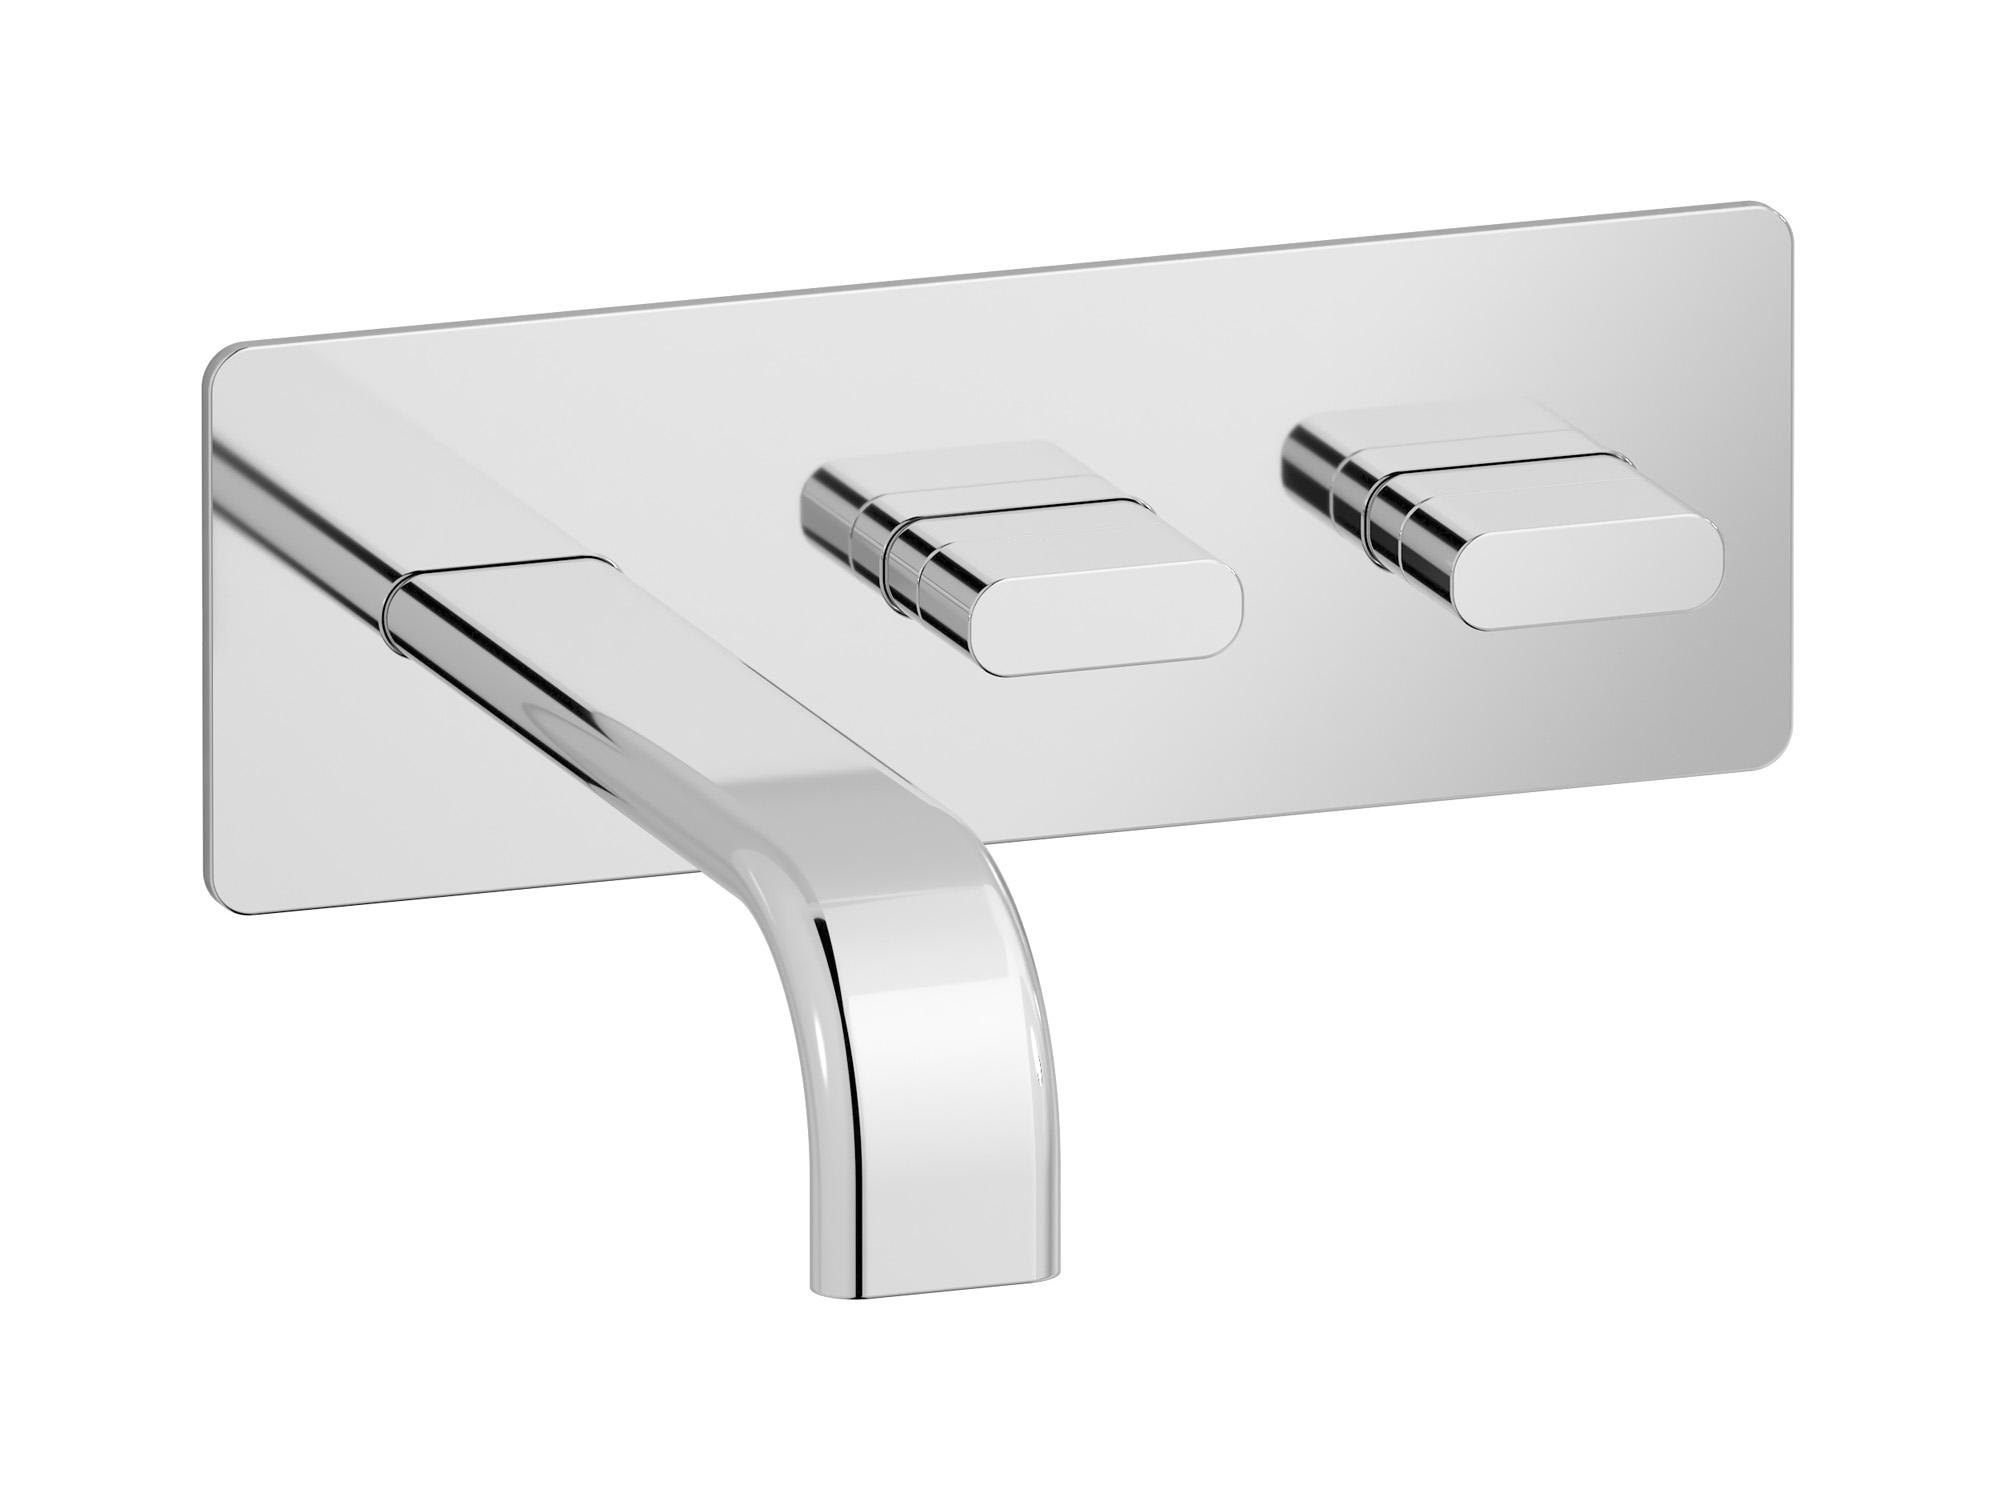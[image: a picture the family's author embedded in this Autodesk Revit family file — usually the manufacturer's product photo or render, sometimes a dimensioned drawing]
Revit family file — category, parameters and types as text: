
# Revit family: SB306
name_source: partatom
category: Apparecchi idraulici
units: mm (PartAtom-declared; Revit-internal decimal feet)

## family parameters
Basato su piano di lavoro = No
Condiviso = No
Mantieni orientamento annotazione = No
Numero OmniClass = 23.45.55.17
Punto di calcolo locali = No
Quota connettore circolare = Usa diametro
Sempre verticale = Sì
Taglio con vuoti quando caricato = No
Tipo di parte = Normale
Titolo OmniClass = Mixing Faucets

## types (6) — shared parameters
Cold water inlet = 10 mm  [stored 0.0328084 ft]
Commenti sul tipo = Lavatory faucet
Connessione CW = No
Connessione HW = No
Connessione di scarico = No
Connessione di ventilazione = No
Descrizione = Wall mounted widespread lavatory faucet
Hot water inlet = 10 mm  [stored 0.0328084 ft]
Produttore = IB Rubinetterie S.p.A.
URL = https://www.weareib.it
zero-valued in all types: Prospetto di default

## per-type parameters (varying)
| type | Finishes surface | Immagine tipo | Modello |
| Chrome | IB_Chrome | SB306CC.jpg | SB306CC |
| Brushed nickel | IB_Brushed nickel | SB306SS.jpg | SB306SS |
| Matt black | IB_matt black | SB306NP.jpg | SB306NP |
| Brushed gold | IB_brushed gold | SB306OS.jpg | SB306OS |
| Rose gold | IB_Rose gold | SB306RS.jpg | SB306RS |
| Natural brass | IB_Brass | SB306ON.jpg | SB306ON |

note: [stored X ft] marks values corroborated as IEEE doubles in the binary element streams (Revit-internal decimal feet)
